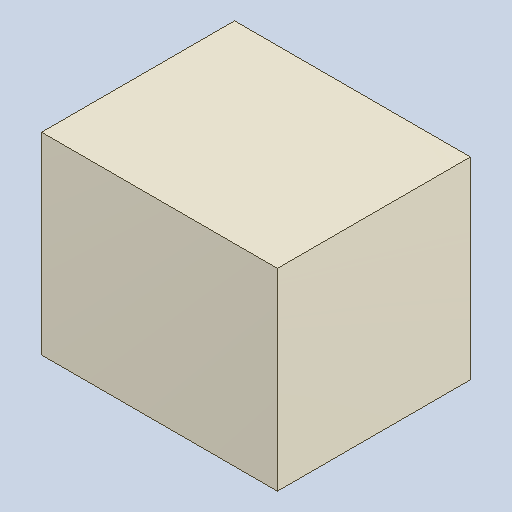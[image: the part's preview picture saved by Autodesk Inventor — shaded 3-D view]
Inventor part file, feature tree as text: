
AUTODESK INVENTOR PART (.ipt)
format: ipt  version: 2023.4 (Build 274418000, 418)  size: 81,920 bytes
history: native  units: mm
features: extrude x1
ambient origin geometry x8: Origin, YZ Plane, XZ Plane, XY Plane, X Axis, Y Axis, Z Axis, Center Point
bodies: Solid1 (feature_tree)
feature tree (1):
  extrude  "Extruded_5"  [1 undecoded]
note: 1 required parameter value undecoded (feature->parameter linkage not recoverable at this tier; creation-order binding heuristic only, values carry confidence <= 0.55)
